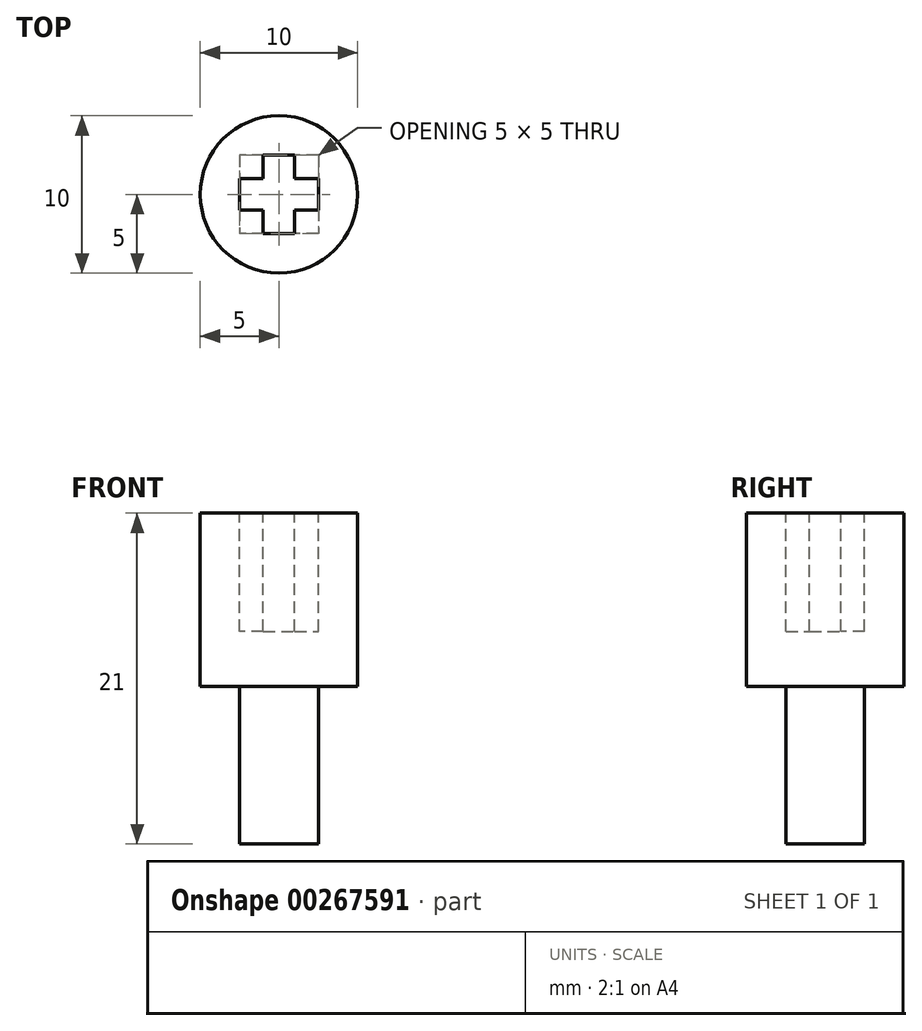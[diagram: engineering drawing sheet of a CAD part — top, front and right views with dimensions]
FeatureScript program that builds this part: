
annotation { "Feature Type Name" : "Feature", "Feature Type Description" : "" }
export const myFeature = defineFeature(function(context is Context, id is Id, definition is map)
    precondition{}
    {
        {
            var Q0;
            Q0=qCreatedBy(makeId("Top.planeOp"),FACE);
            var sketch = newSketch(context, id + "F0", { "sketchPlane" : qUnion([Q0])});
            skLineSegment(sketch, "E0.bottom", {"start": v(2.5, 2.5) * mm, "end": v(-2.5, 2.5) * mm});
            skLineSegment(sketch, "E0.top", {"start": v(2.5, -2.5) * mm, "end": v(-2.5, -2.5) * mm});
            skLineSegment(sketch, "E0.left", {"start": v(2.5, 2.5) * mm, "end": v(2.5, -2.5) * mm});
            skLineSegment(sketch, "E0.right", {"start": v(-2.5, 2.5) * mm, "end": v(-2.5, -2.5) * mm});
            skPoint(sketch, "E0.middle", {"position": v(0, 0) * mm});
            skSolve(sketch);
        }
        {
            var Q0;
            Q0=makeQuery(id+"F0.imprint","IMPRINT",FACE,{"disambiguationData":[TD([[makeQuery(id+"F0.imprint","IMPRINT",EDGE,{"derivedFrom":sQuery(id+"F0.wireOp",EDGE,"E0.bottom")}),1.0]])]});
            extrude(context, id + "F1", {"entities" : qUnion([Q0]), "depth" : 10 * mm});
        }
        {
            var Q0;
            Q0=makeQuery(id+"F1.opExtrude","CAP_FACE",FACE,{"disambiguationData":[OSD([sQuery(id+"F0.wireOp",EDGE,"E0.bottom"),sQuery(id+"F0.wireOp",EDGE,"E0.top"),sQuery(id+"F0.wireOp",EDGE,"E0.left"),sQuery(id+"F0.wireOp",EDGE,"E0.right")])],"isStart":false});
            var sketch = newSketch(context, id + "F2", { "sketchPlane" : qUnion([Q0])});
            skCircle(sketch, "E1", {"center": v(0, 0) * mm, "radius": 5 * mm});
            skSolve(sketch);
        }
        {
            var Q0;
            Q0=makeQuery(id+"F2.imprint","IMPRINT",FACE,{"disambiguationData":[TD([[makeQuery(id+"F2.imprint","IMPRINT",EDGE,{"derivedFrom":sQuery(id+"F2.wireOp",EDGE,"E1")}),1.0]])]});
            var Q1;
            Q1=makeQuery(id+"F2.imprint","IMPRINT",FACE,{"disambiguationData":[TD([[makeQuery(id+"F2.imprint","IMPRINT",EDGE,{"derivedFrom":makeQuery(id+"F1.opExtrude","CAP_EDGE",EDGE,{"disambiguationData":[OSD([sQuery(id+"F0.wireOp",EDGE,"E0.bottom")])],"isStart":false})}),1.0]])]});
            extrude(context, id + "F3", {"entities" : qUnion([Q0, Q1]), "operationType" : NewBodyOperationType.ADD, "depth" : 11 * mm});
        }
        {
            var Q0;
            Q0=makeQuery(id+"F3.opExtrude","CAP_FACE",FACE,{"disambiguationData":[OSD([sQuery(id+"F2.wireOp",EDGE,"E1")])],"isStart":false});
            var sketch = newSketch(context, id + "F4", { "sketchPlane" : qUnion([Q0])});
            skLineSegment(sketch, "E2", {"start": v(-1, 2.5) * mm, "end": v(-1, 1) * mm});
            skLineSegment(sketch, "E3", {"start": v(-1, 1) * mm, "end": v(-2.5, 1) * mm});
            skLineSegment(sketch, "E4", {"start": v(0, 5) * mm, "end": v(0, -5) * mm, "construction": true});
            skLineSegment(sketch, "E5.MirrorCS", {"start": v(1, 2.5) * mm, "end": v(1, 1) * mm});
            skLineSegment(sketch, "E6.MirrorCS", {"start": v(1, 1) * mm, "end": v(2.5, 1) * mm});
            skLineSegment(sketch, "E7", {"start": v(-5, 0) * mm, "end": v(5, 0) * mm, "construction": true});
            skLineSegment(sketch, "E8.MirrorCS", {"start": v(-1, -1) * mm, "end": v(-2.5, -1) * mm});
            skLineSegment(sketch, "E9.MirrorCS", {"start": v(-1, -2.5) * mm, "end": v(-1, -1) * mm});
            skLineSegment(sketch, "E10.MirrorCS", {"start": v(1, -1) * mm, "end": v(2.5, -1) * mm});
            skLineSegment(sketch, "E11.MirrorCS", {"start": v(1, -2.5) * mm, "end": v(1, -1) * mm});
            skLineSegment(sketch, "E12", {"start": v(-2.5, -1) * mm, "end": v(-2.5, 1) * mm});
            skLineSegment(sketch, "E13", {"start": v(-1, 2.5) * mm, "end": v(1, 2.5) * mm});
            skLineSegment(sketch, "E14", {"start": v(2.5, 1) * mm, "end": v(2.5, -1) * mm});
            skLineSegment(sketch, "E15", {"start": v(1, -2.5) * mm, "end": v(-1, -2.5) * mm});
            skSolve(sketch);
        }
        {
            var Q0;
            Q0=makeQuery(id+"F4.imprint","IMPRINT",FACE,{"disambiguationData":[TD([[makeQuery(id+"F4.imprint","IMPRINT",EDGE,{"derivedFrom":sQuery(id+"F4.wireOp",EDGE,"E2")}),1.0]])]});
            extrude(context, id + "F5", {"entities" : qUnion([Q0]), "operationType" : NewBodyOperationType.REMOVE, "oppositeDirection" : true, "depth" : 7.5 * mm});
        }
    });
